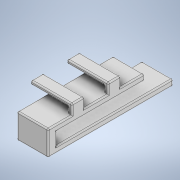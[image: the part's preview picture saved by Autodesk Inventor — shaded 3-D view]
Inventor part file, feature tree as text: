
AUTODESK INVENTOR PART (.ipt)
format: ipt  version: 2020 (Build 240168000, 168)  size: 261,120 bytes
history: native  units: in
note: dims shown in document units (in); Inventor stores cm internally (conversion verified against a paired STEP export)
features: extrude x5, sketch x5, fillet x2
ambient origin geometry x8: Origin, YZ Plane, XZ Plane, XY Plane, X Axis, Y Axis, Z Axis, Center Point
bodies: Solid1 (feature_tree)
feature tree (12):
  extrude  "Extrusion1"  Depth=1.0in
  extrude  "Extrusion2"  Depth=0.15in TaperAngle=0.0deg
  extrude  "Extrusion3"  Depth=0.08in TaperAngle=0.0deg
  extrude  "Extrusion4"  Depth=0.19in
  fillet  "Fillet1"  Radius=0.03in
  extrude  "Extrusion6"  Depth=0.19in
  fillet  "Fillet2"  Radius=0.03in
  sketch  "Sketch1"  dims[d0=0.25in d1=1.0in]
  sketch  "Sketch2"  dims[d2=0.05in d3=0.0in d4=0.15in d5=0.0in]
  sketch  "Sketch4"  dims[d6=0.7in d7=0.0in d14=0.08in d15=0.0in]
  sketch  "Sketch5"  dims[d20=0.01in d21=0.19in d22=0.03in]
  sketch  "Sketch7"  dims[d23=0.1in d24=0.19in d25=0.03in d26=0.1in d27=0.1in d28=0.03in d29=0.1in d30=0.03in d31=0.3in d32=0.0in d33=0.01in d16=0.5in d17=0.0344in]
